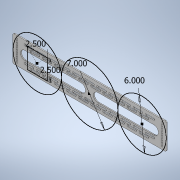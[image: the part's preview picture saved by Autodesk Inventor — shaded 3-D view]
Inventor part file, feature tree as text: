
AUTODESK INVENTOR PART (.ipt)
format: ipt  version: 2020 (Build 240168000, 168)  size: 599,040 bytes
history: native  units: in
note: dims shown in document units (in); Inventor stores cm internally (conversion verified against a paired STEP export)
features: sketch x2, extrude x1, fillet x1
ambient origin geometry x8: Origin, YZ Plane, XZ Plane, XY Plane, X Axis, Y Axis, Z Axis, Center Point
bodies: Solid1 (feature_tree)
feature tree (4):
  extrude  "Extrusion1"  Depth=3.25in
  sketch  "Sketch2"  dims[d3=1.75in d4=0.101in d5=1.0in d6=2.0in d7=1.5in d8=1.25in d9=4.3307in d11=1.5in d12=0.3937in d14=1.0in d16=0.75in d17=2.0in d18=0.3in d19=0.95in d20=3.937in d22=1.5in d23=0.3937in d25=1.0in d34=0.55in d35=1.15in d38=1.05in d47=0.125in d48=0.0in d49=7.0in d51=6.0in d53=2.5in d54=2.5in d62=0.5in d63=0.201in d64=0.375in d65=4.3307in d67=0.25in d68=0.7874in d70=18.0in d73=0.125in]
  fillet  "Fillet1"  Radius=9.5in
  sketch  "Sketch1"  dims[d0=19.0in d1=3.25in d2=9.5in]
